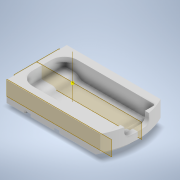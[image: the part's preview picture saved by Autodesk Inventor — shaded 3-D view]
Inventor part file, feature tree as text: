
AUTODESK INVENTOR PART (.ipt)
format: ipt  version: 2021 (Build 250183000, 183)  size: 851,456 bytes
history: native  units: in
note: dims shown in document units (in); Inventor stores cm internally (conversion verified against a paired STEP export)
features: sketch x10, extrude x9, fillet x5, chamfer x3, plane x3, mirror x2, other x1, pattern_circular x1
ambient origin geometry x8: Origin, YZ Plane, XZ Plane, XY Plane, X Axis, Y Axis, Z Axis, Center Point
bodies: Solid1 (feature_tree)
feature tree (34):
  extrude  "Extrusion1"  Depth=0.315in TaperAngle=0.0deg
  chamfer  "Chamfer2"  Distance=0.189in
  extrude  "Extrusion2"  Depth=0.1614in
  extrude  "Extrusion3"  Depth=0.2205in
  other  "Work Axis1"
  plane  "Work Plane1"
  extrude  "Extrusion5"  Depth=0.8268in
  extrude  "Extrusion4"  Depth=0.1969in
  fillet  "Fillet4"  Radius=0.063in
  pattern_circular  "Circular Pattern2"  [2 undecoded]
  fillet  "Fillet7"  [1 undecoded]
  extrude  "Extrusion9"  Depth=0.0394in
  extrude  "Extrusion10"  Depth=0.1181in TaperAngle=240.0deg
  fillet  "Fillet9"  Radius=0.0315in
  fillet  "Fillet10"  Radius=1.1811in
  mirror  "Mirror6"
  sketch  "Sketch18"  dims[d18=0.2047in d19=0.0in d23=0.8268in]
  chamfer  "Chamfer4"  Distance=0.5906in
  chamfer  "Chamfer5"  Distance=0.9728in
  fillet  "Fillet11"  Radius=0.4864in
  plane  "Work Plane5"
  extrude  "Extrusion13"  Depth=0.0394in TaperAngle=0.0deg
  mirror  "Mirror7"
  plane  "Work Plane6"
  extrude  "Extrusion14"  Depth=0.547in
  sketch  "Sketch1"  dims[d0=2.0472in d3=0.315in d4=0.0in]
  sketch  "Sketch2"  dims[d5=1.4276in]
  sketch  "Sketch3"  dims[d6=0.7079in]
  sketch  "Sketch4"  dims[d7=0.3539in]
  sketch  "Sketch7"  dims[d8=0.4843in d9=0.189in d10=0.0in]
  sketch  "Sketch12"  dims[d11=0.0in d14=0.1614in]
  sketch  "Sketch13"  dims[d15=0.0in d16=0.0in d17=0.2205in]
  sketch  "Sketch19"  dims[d24=0.3539in d31=0.1969in d32=0.063in d33=0.0in]
  sketch  "Sketch20"  dims[d44=0.1614in d47=0.0433in d48=0.0in d49=0.0in d51=0.0in d54=0.063in d55=0.0in d56=45.0deg d58=0.0394in d59=0.1181in d60=1.9685in d61=240.0deg d72=0.0315in d80=1.1811in d81=0.5906in d82=0.9728in d83=0.4864in d84=0.0394in d85=0.0in d86=0.547in d87=0.2735in d88=0.0787in d89=0.0in d90=0.0787in d98=0.1024in d99=0.0in d100=0.0in d101=0.2362in d102=0.0315in d103=0.0315in d104=0.2953in d105=0.1575in d106=0.1969in d107=0.063in d108=0.0787in d109=45.0deg d110=0.063in d111=0.0787in d112=45.0deg d113=0.1063in d114=0.4724in d115=0.0in d116=0.0in d117=-0.0787in d118=0.3937in d119=0.0in d91=0.0197in d92=0.0344in d93=0.0197in d94=0.0344in]
note: 3 required parameter values undecoded (feature->parameter linkage not recoverable at this tier; creation-order binding heuristic only, values carry confidence <= 0.55)
